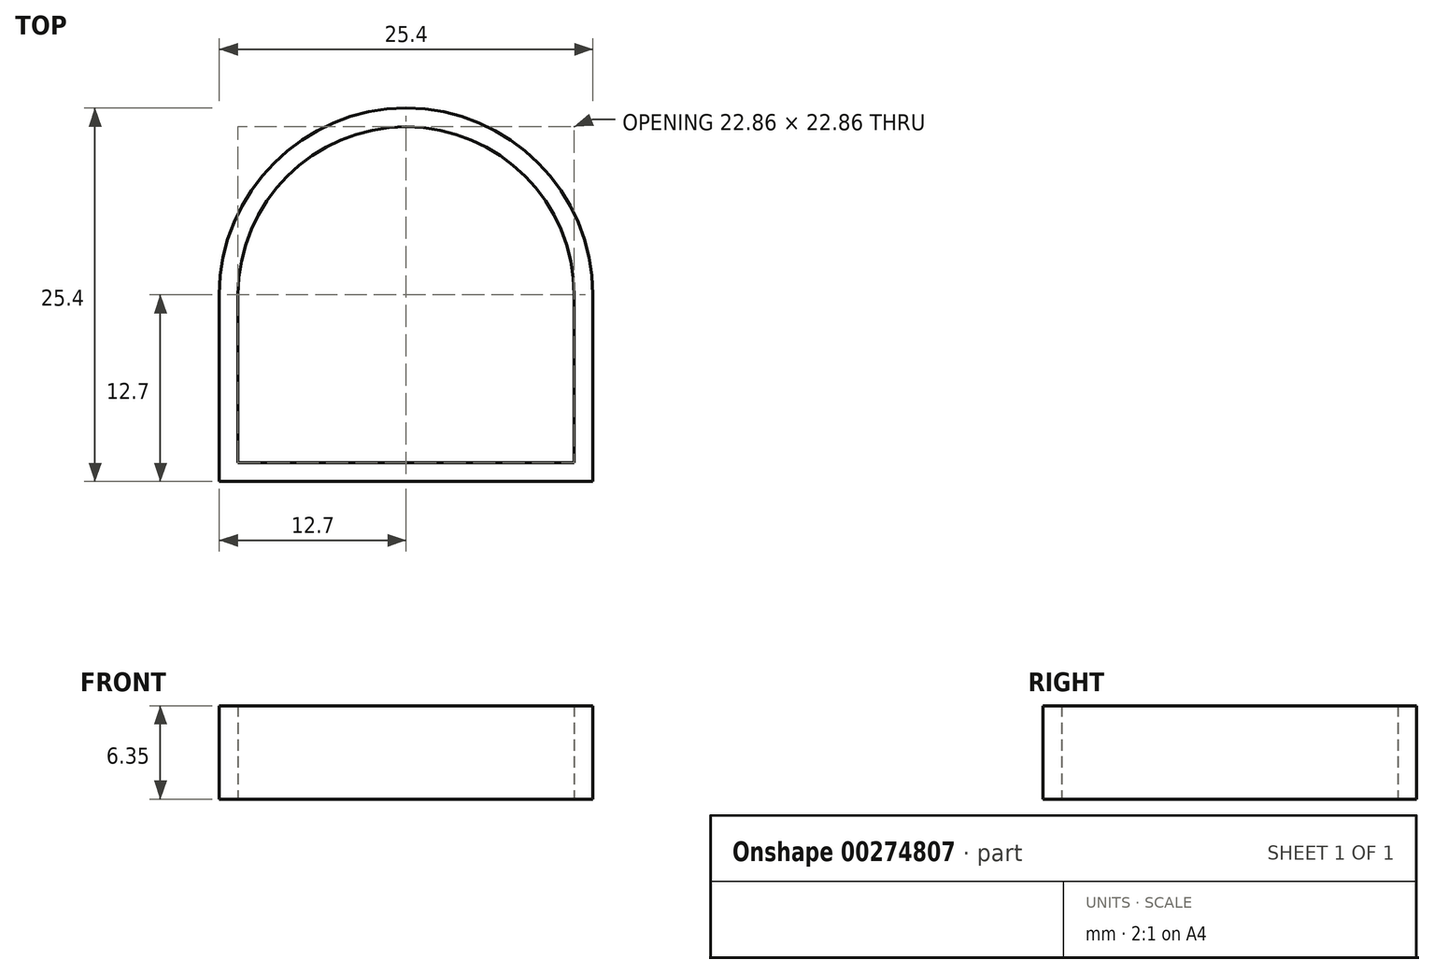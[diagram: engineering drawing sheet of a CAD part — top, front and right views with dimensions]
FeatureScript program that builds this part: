
annotation { "Feature Type Name" : "Feature", "Feature Type Description" : "" }
export const myFeature = defineFeature(function(context is Context, id is Id, definition is map)
    precondition{}
    {
        {
            var Q0;
            Q0=qCreatedBy(makeId("Top.planeOp"),FACE);
            var sketch = newSketch(context, id + "F0", { "sketchPlane" : qUnion([Q0])});
            skLineSegment(sketch, "E0.bottom", {"start": v(0, 0) * mm, "end": v(25.4, 0) * mm});
            skLineSegment(sketch, "E0.left", {"start": v(0, 0) * mm, "end": v(0, 12.7) * mm});
            skLineSegment(sketch, "E0.right", {"start": v(25.4, 0) * mm, "end": v(25.4, 12.7) * mm});
            skArc(sketch, "E1", {"start": v(25.4, 12.7) * mm, "mid": v(12.7, 25.4) * mm, "end": v(0, 12.7) * mm});
            skArc(sketch, "E2.0", {"start": v(24.13, 12.7) * mm, "mid": v(12.7, 24.13) * mm, "end": v(1.27, 12.7) * mm});
            skLineSegment(sketch, "E2.1", {"start": v(24.13, 1.27) * mm, "end": v(24.13, 12.7) * mm});
            skLineSegment(sketch, "E2.2", {"start": v(1.27, 1.27) * mm, "end": v(24.13, 1.27) * mm});
            skLineSegment(sketch, "E2.3", {"start": v(1.27, 1.27) * mm, "end": v(1.27, 12.7) * mm});
            skSolve(sketch);
        }
        {
            var Q0;
            Q0 = qSketchRegion(id + "F0", true);
            extrude(context, id + "F1", {"entities" : qUnion([Q0]), "depth" : 6.35 * mm});
        }
    });
